# Revit family: Faucet-Single_Control-American_Standard-Aspirations-7061104_Series
name_source: partatom
category: Plumbing Fixtures
units: mm (PartAtom-declared; Revit-internal decimal feet)

## family parameters
Always vertical = No
Cut with Voids When Loaded = No
OmniClass Number = 23.45.55.14
OmniClass Title = Single Faucets
Part Type = Normal
Room Calculation Point = No
Round Connector Dimension = Use Diameter
Shared = Yes
Work Plane-Based = Yes

## types (3) — shared parameters
70204P0 Escutcheon Plate = Yes
ANSI A117.1 = Yes
ASME A112.18.1/CSA B125.1 = Yes
Assembly Code = D2020300
CW Connection = No
CWFU = 1.5
Compliance Certifications = These products meet or exceed the following codes and standards: ANSI A117.1, ASME A112.18.1, NSF 61/Section 9 & Annex G, CSA B125
Default Elevation = 0"
Description = Aspirations™ Single Control Lavatory Faucet
Faucet Height Position = 5/16"
HW Connection = No
HWFU = 1.5
Height = 6 3/8"
Installation Type = Deck Mounted
Length = 6 11/16"
Manufacturer = American Standard
Max. Flow Rate = 1.2 gpm/4.5 L/min.
NSF/ANSI/CAN 372 = Yes
NSF/ANSI/CAN 61 = Yes
Tempered Water Connection = Yes
Tempered Water Connection Diameter = 3/8"
URL = http://www.americanstandard-us.com
Vent Connection = No
WFU = 2
Waste Connection = No
Width = 2 3/16"

## per-type parameters (varying)
| type | ADA Compliant | Finish | Material |
| 7061104.002 | Yes | Brass-American Standard-002-Polished Chrome | Brass-American Standard-002-Polished Chrome |
| 7061104.295 | No | Brass-American Standard-295-PVD Brushed Nickel | Brass-American Standard-295-PVD Brushed Nickel |
| 7061104.243 | No | Brass-American Standard-243-Matte Black | Brass-American Standard-243-Matte Black |

note: column(s) folded — value = type name in every type: Model

## geometry (parser evidence)
native form markers: Sweep x3
no freeform markers — native parametric forms only
